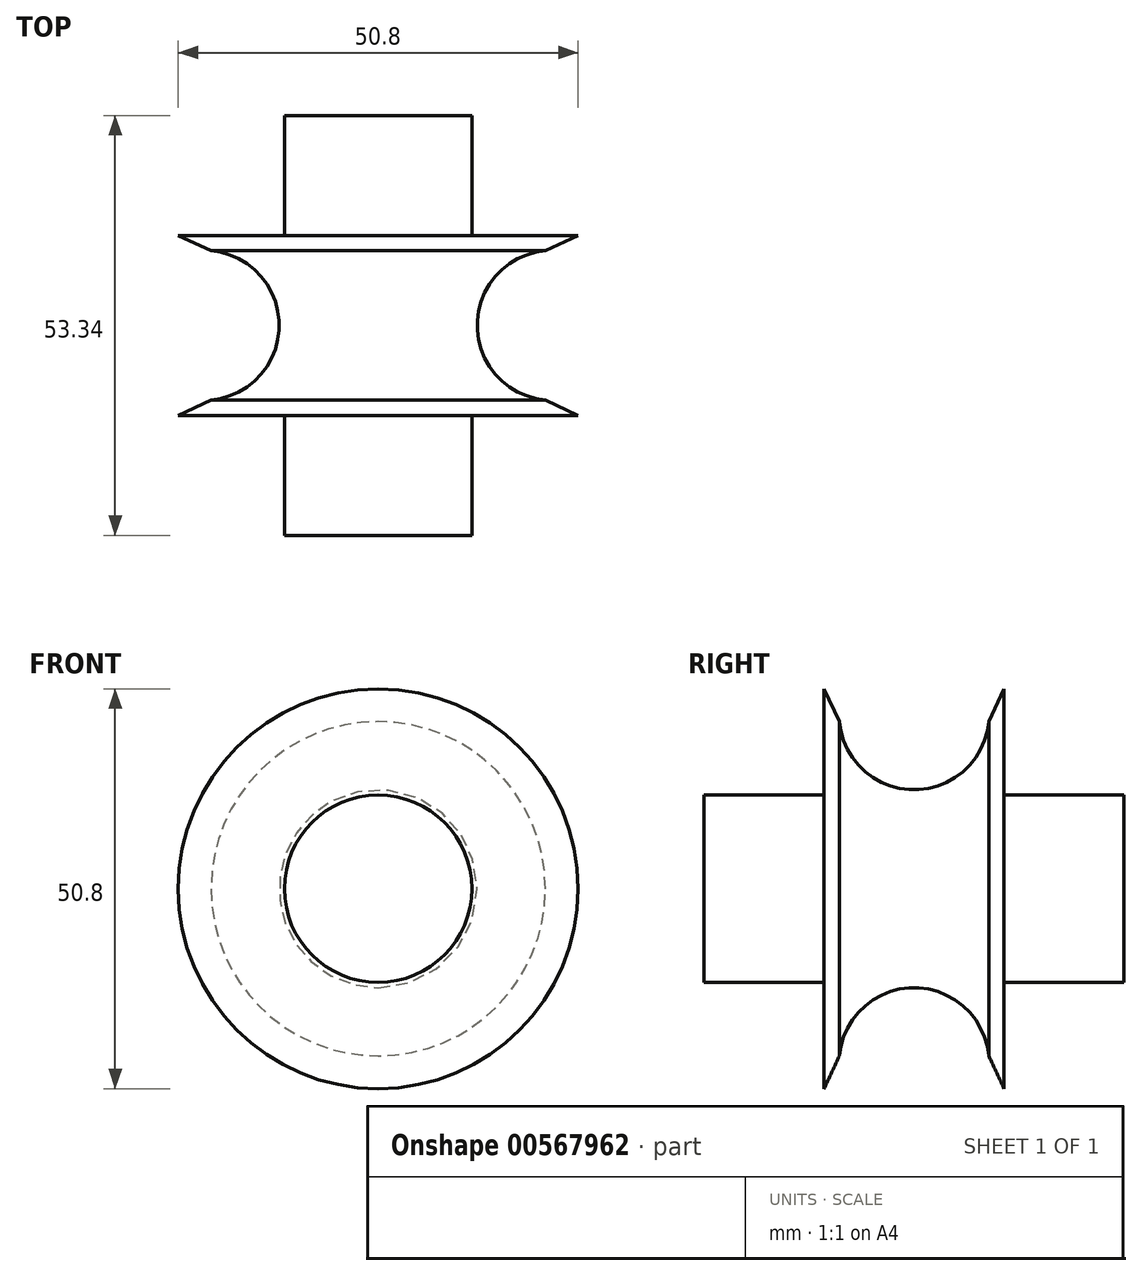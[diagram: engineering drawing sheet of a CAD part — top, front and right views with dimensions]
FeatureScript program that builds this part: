
annotation { "Feature Type Name" : "Feature", "Feature Type Description" : "" }
export const myFeature = defineFeature(function(context is Context, id is Id, definition is map)
    precondition{}
    {
        {
            var Q0;
            Q0=qCreatedBy(makeId("Right.planeOp"),FACE);
            var sketch = newSketch(context, id + "F0", { "sketchPlane" : qUnion([Q0])});
            skLineSegment(sketch, "E0", {"start": v(-11.43, 25.4) * mm, "end": v(-11.43, 0) * mm});
            skLineSegment(sketch, "E1", {"start": v(-11.43, 11.9) * mm, "end": v(-26.67, 11.9) * mm});
            skLineSegment(sketch, "E2", {"start": v(-11.43, 25.4) * mm, "end": v(-9.49, 21.23) * mm});
            skLineSegment(sketch, "E3.MirrorCS", {"start": v(11.43, 25.4) * mm, "end": v(9.49, 21.23) * mm});
            skLineSegment(sketch, "E4.MirrorCS", {"start": v(11.43, 25.4) * mm, "end": v(11.43, 0) * mm});
            skLineSegment(sketch, "E5.MirrorCS", {"start": v(11.43, 11.9) * mm, "end": v(26.67, 11.9) * mm});
            skArc(sketch, "E6", {"start": v(-9.49, 21.23) * mm, "mid": v(0, 12.57) * mm, "end": v(9.49, 21.23) * mm});
            skLineSegment(sketch, "E7", {"start": v(-26.67, 11.9) * mm, "end": v(-26.67, 0) * mm});
            skLineSegment(sketch, "E8", {"start": v(-26.67, 0) * mm, "end": v(26.67, 0) * mm});
            skLineSegment(sketch, "E9", {"start": v(26.67, 0) * mm, "end": v(26.67, 11.9) * mm});
            skSolve(sketch);
        }
        {
            var Q0;
            {var subQ2=sQuery(id+"F0.wireOp",EDGE,"E1");Q0=makeQuery(id+"F0.imprint","IMPRINT",FACE,{"disambiguationData":[TD([[makeQuery(id+"F0.imprint","IMPRINT",EDGE,{"derivedFrom":subQ2}),1.0]])]});}
            var Q1;
            {var subQ1=sQuery(id+"F0.wireOp",EDGE,"E2");Q1=makeQuery(id+"F0.imprint","IMPRINT",FACE,{"disambiguationData":[TD([[makeQuery(id+"F0.imprint","IMPRINT",EDGE,{"derivedFrom":subQ1}),-1.0]])]});}
            var Q2;
            {var subQ3=sQuery(id+"F0.wireOp",EDGE,"E5.MirrorCS");Q2=makeQuery(id+"F0.imprint","IMPRINT",FACE,{"disambiguationData":[TD([[makeQuery(id+"F0.imprint","IMPRINT",EDGE,{"derivedFrom":subQ3}),-1.0]])]});}
            var Q3;
            Q3=sQuery(id+"F0.wireOp",EDGE,"E8");
            revolve(context, id + "F1", {"entities" : qUnion([Q0, Q1, Q2]), "axis" : qUnion([Q3]), "revolveType" : RevolveType.FULL});
        }
    });
